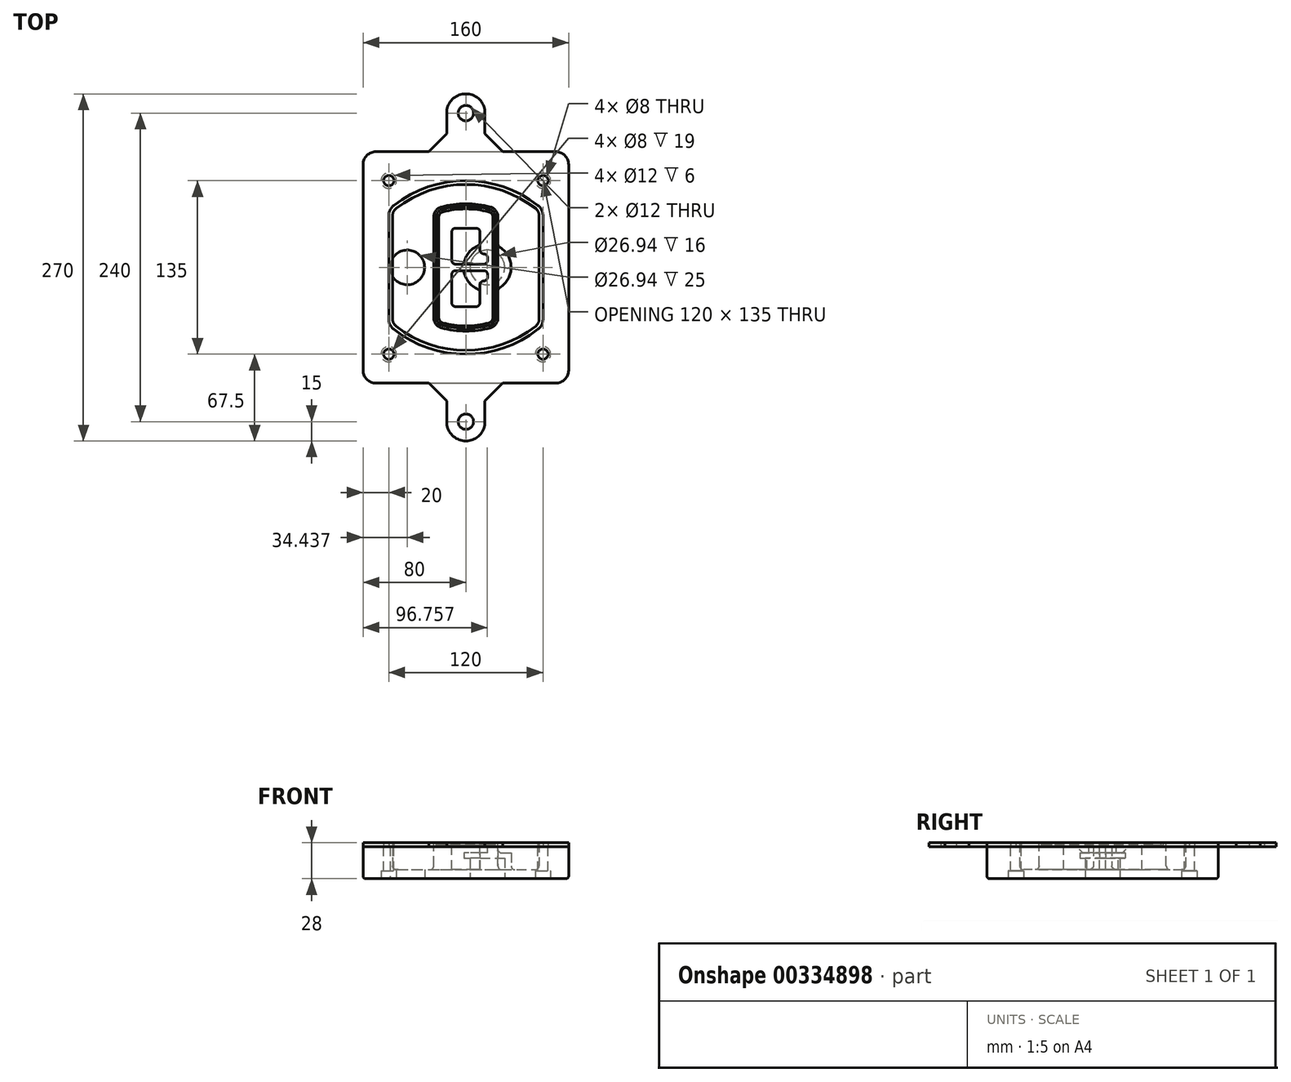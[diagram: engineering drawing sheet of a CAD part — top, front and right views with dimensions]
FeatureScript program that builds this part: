
annotation { "Feature Type Name" : "Feature", "Feature Type Description" : "" }
export const myFeature = defineFeature(function(context is Context, id is Id, definition is map)
    precondition{}
    {
        {
            var Q0;
            Q0=qCreatedBy(makeId("Top.planeOp"),FACE);
            var sketch = newSketch(context, id + "F0", { "sketchPlane" : qUnion([Q0])});
            skPoint(sketch, "E0.rect.middle", {"position": v(0, 0) * mm});
            skLineSegment(sketch, "E1.bottom", {"start": v(-70, -90) * mm, "end": v(70, -90) * mm});
            skLineSegment(sketch, "E1.top", {"start": v(-70, 90) * mm, "end": v(70, 90) * mm});
            skLineSegment(sketch, "E1.left", {"start": v(-80, -80) * mm, "end": v(-80, 80) * mm});
            skLineSegment(sketch, "E1.right", {"start": v(80, -80) * mm, "end": v(80, 80) * mm});
            skLineSegment(sketch, "E2", {"start": v(-80, 90) * mm, "end": v(80, -90) * mm, "construction": true});
            skLineSegment(sketch, "E3", {"start": v(80, 90) * mm, "end": v(-80, -90) * mm, "construction": true});
            skCircle(sketch, "E4", {"center": v(-60, 67.5) * mm, "radius": 4 * mm});
            skCircle(sketch, "E5", {"center": v(60, 67.5) * mm, "radius": 4 * mm});
            skCircle(sketch, "E6", {"center": v(60, -67.5) * mm, "radius": 4 * mm});
            skCircle(sketch, "E7", {"center": v(-60, -67.5) * mm, "radius": 4 * mm});
            skLineSegment(sketch, "E8", {"start": v(-60, 67.5) * mm, "end": v(60, 67.5) * mm, "construction": true});
            skLineSegment(sketch, "E9", {"start": v(60, 67.5) * mm, "end": v(60, -67.5) * mm, "construction": true});
            skLineSegment(sketch, "E10", {"start": v(60, -67.5) * mm, "end": v(-60, -67.5) * mm, "construction": true});
            skLineSegment(sketch, "E11", {"start": v(-60, -67.5) * mm, "end": v(-60, 67.5) * mm, "construction": true});
            skLineSegment(sketch, "E12", {"start": v(-60, 40.3) * mm, "end": v(-60, -40.3) * mm});
            skLineSegment(sketch, "E13", {"start": v(60, 40.3) * mm, "end": v(60, -40.3) * mm});
            skArc(sketch, "E14", {"start": v(56.15, 48.18) * mm, "mid": v(0, 67.5) * mm, "end": v(-56.15, 48.18) * mm});
            skArc(sketch, "E15", {"start": v(-56.15, -48.18) * mm, "mid": v(0, -67.5) * mm, "end": v(56.15, -48.18) * mm});
            skLineSegment(sketch, "E16", {"start": v(-60, 0) * mm, "end": v(60, 0) * mm, "construction": true});
            skPoint(sketch, "E17.visualSharp", {"position": v(-60, -45) * mm});
            skArc(sketch, "E17.filletArc", {"start": v(-60, -40.3) * mm, "mid": v(-58.99, -44.68) * mm, "end": v(-56.15, -48.18) * mm});
            skPoint(sketch, "E18.visualSharp", {"position": v(-60, 45) * mm});
            skArc(sketch, "E18.filletArc", {"start": v(-56.15, 48.18) * mm, "mid": v(-58.99, 44.68) * mm, "end": v(-60, 40.3) * mm});
            skPoint(sketch, "E19.visualSharp", {"position": v(60, 45) * mm});
            skArc(sketch, "E19.filletArc", {"start": v(60, 40.3) * mm, "mid": v(58.99, 44.68) * mm, "end": v(56.15, 48.18) * mm});
            skPoint(sketch, "E20.visualSharp", {"position": v(60, -45) * mm});
            skArc(sketch, "E20.filletArc", {"start": v(56.15, -48.18) * mm, "mid": v(58.99, -44.68) * mm, "end": v(60, -40.3) * mm});
            skPoint(sketch, "E21.visualSharp", {"position": v(-80, 90) * mm});
            skArc(sketch, "E21.filletArc", {"start": v(-70, 90) * mm, "mid": v(-77.07, 87.07) * mm, "end": v(-80, 80) * mm});
            skPoint(sketch, "E22.visualSharp", {"position": v(80, 90) * mm});
            skArc(sketch, "E22.filletArc", {"start": v(80, 80) * mm, "mid": v(77.07, 87.07) * mm, "end": v(70, 90) * mm});
            skPoint(sketch, "E23.visualSharp", {"position": v(80, -90) * mm});
            skArc(sketch, "E23.filletArc", {"start": v(70, -90) * mm, "mid": v(77.07, -87.07) * mm, "end": v(80, -80) * mm});
            skPoint(sketch, "E24.visualSharp", {"position": v(-80, -90) * mm});
            skArc(sketch, "E24.filletArc", {"start": v(-80, -80) * mm, "mid": v(-77.07, -87.07) * mm, "end": v(-70, -90) * mm});
            skArc(sketch, "E25.0", {"start": v(57, 40.3) * mm, "mid": v(56.3, 43.36) * mm, "end": v(54.3, 45.81) * mm});
            skLineSegment(sketch, "E25.1", {"start": v(57, 40.3) * mm, "end": v(57, -40.3) * mm});
            skArc(sketch, "E25.2", {"start": v(54.3, -45.81) * mm, "mid": v(56.3, -43.36) * mm, "end": v(57, -40.3) * mm});
            skArc(sketch, "E25.3", {"start": v(-54.3, -45.81) * mm, "mid": v(0, -64.5) * mm, "end": v(54.3, -45.81) * mm});
            skArc(sketch, "E25.4", {"start": v(-57, -40.3) * mm, "mid": v(-56.3, -43.36) * mm, "end": v(-54.3, -45.81) * mm});
            skArc(sketch, "E25.5", {"start": v(54.3, 45.81) * mm, "mid": v(0, 64.5) * mm, "end": v(-54.3, 45.81) * mm});
            skLineSegment(sketch, "E25.6", {"start": v(-57, 40.3) * mm, "end": v(-57, -40.3) * mm});
            skArc(sketch, "E25.7", {"start": v(-54.3, 45.81) * mm, "mid": v(-56.3, 43.36) * mm, "end": v(-57, 40.3) * mm});
            skArc(sketch, "E26.0", {"start": v(-58.62, 51.33) * mm, "mid": v(-62.58, 46.43) * mm, "end": v(-64, 40.3) * mm});
            skArc(sketch, "E26.1", {"start": v(58.62, 51.33) * mm, "mid": v(0, 71.5) * mm, "end": v(-58.62, 51.33) * mm});
            skArc(sketch, "E26.2", {"start": v(64, 40.3) * mm, "mid": v(62.58, 46.43) * mm, "end": v(58.62, 51.33) * mm});
            skLineSegment(sketch, "E26.3", {"start": v(64, 40.3) * mm, "end": v(64, -40.3) * mm});
            skArc(sketch, "E26.4", {"start": v(58.62, -51.33) * mm, "mid": v(62.58, -46.43) * mm, "end": v(64, -40.3) * mm});
            skLineSegment(sketch, "E26.5", {"start": v(-64, 40.3) * mm, "end": v(-64, -40.3) * mm});
            skArc(sketch, "E26.6", {"start": v(-58.62, -51.33) * mm, "mid": v(0, -71.5) * mm, "end": v(58.62, -51.33) * mm});
            skArc(sketch, "E26.7", {"start": v(-64, -40.3) * mm, "mid": v(-62.58, -46.43) * mm, "end": v(-58.62, -51.33) * mm});
            skSolve(sketch);
        }
        {
            var Q0;
            Q0=makeQuery(id+"F0.imprint","IMPRINT",FACE,{"disambiguationData":[TD([[makeQuery(id+"F0.imprint","IMPRINT",EDGE,{"derivedFrom":sQuery(id+"F0.wireOp",EDGE,"E1.bottom")}),1.0]])]});
            var Q1;
            Q1=makeQuery(id+"F0.imprint","IMPRINT",FACE,{"disambiguationData":[TD([[makeQuery(id+"F0.imprint","IMPRINT",EDGE,{"derivedFrom":sQuery(id+"F0.wireOp",EDGE,"E12")}),1.0]])]});
            var Q2;
            Q2=makeQuery(id+"F0.imprint","IMPRINT",FACE,{"disambiguationData":[TD([[makeQuery(id+"F0.imprint","IMPRINT",EDGE,{"derivedFrom":sQuery(id+"F0.wireOp",EDGE,"E25.0")}),1.0]])]});
            var Q3;
            Q3=makeQuery(id+"F0.imprint","IMPRINT",FACE,{"disambiguationData":[TD([[makeQuery(id+"F0.imprint","IMPRINT",EDGE,{"derivedFrom":sQuery(id+"F0.wireOp",EDGE,"E12")}),-1.0]])]});
            extrude(context, id + "F1", {"entities" : qUnion([Q0, Q1, Q2, Q3]), "oppositeDirection" : true, "depth" : 25 * mm});
        }
        {
            var Q0;
            Q0=makeQuery(id+"F0.imprint","IMPRINT",FACE,{"disambiguationData":[TD([[makeQuery(id+"F0.imprint","IMPRINT",EDGE,{"derivedFrom":sQuery(id+"F0.wireOp",EDGE,"E12")}),1.0]])]});
            extrude(context, id + "F2", {"entities" : qUnion([Q0]), "operationType" : NewBodyOperationType.ADD, "depth" : 3 * mm});
        }
        {
            var Q0;
            Q0=makeQuery(id+"F0.imprint","IMPRINT",FACE,{"disambiguationData":[TD([[makeQuery(id+"F0.imprint","IMPRINT",EDGE,{"derivedFrom":sQuery(id+"F0.wireOp",EDGE,"E25.0")}),1.0]])]});
            extrude(context, id + "F3", {"entities" : qUnion([Q0]), "operationType" : NewBodyOperationType.REMOVE, "oppositeDirection" : true, "depth" : 18 * mm});
        }
        {
            var Q0;
            Q0=makeQuery(id+"F2.opExtrude","CAP_FACE",FACE,{"disambiguationData":[OSD([sQuery(id+"F0.wireOp",EDGE,"E12"),sQuery(id+"F0.wireOp",EDGE,"E13"),sQuery(id+"F0.wireOp",EDGE,"E14"),sQuery(id+"F0.wireOp",EDGE,"E15"),sQuery(id+"F0.wireOp",EDGE,"E17.filletArc"),sQuery(id+"F0.wireOp",EDGE,"E18.filletArc"),sQuery(id+"F0.wireOp",EDGE,"E19.filletArc"),sQuery(id+"F0.wireOp",EDGE,"E20.filletArc"),sQuery(id+"F0.wireOp",EDGE,"E25.0"),sQuery(id+"F0.wireOp",EDGE,"E25.1"),sQuery(id+"F0.wireOp",EDGE,"E25.2"),sQuery(id+"F0.wireOp",EDGE,"E25.3"),sQuery(id+"F0.wireOp",EDGE,"E25.4"),sQuery(id+"F0.wireOp",EDGE,"E25.5"),sQuery(id+"F0.wireOp",EDGE,"E25.6"),sQuery(id+"F0.wireOp",EDGE,"E25.7")])],"isStart":false});
            var sketch = newSketch(context, id + "F4", { "sketchPlane" : qUnion([Q0])});
            skArc(sketch, "E27.0", {"start": v(-19.08, -46.97) * mm, "mid": v(0, -49.5) * mm, "end": v(19.08, -46.97) * mm});
            skArc(sketch, "E28.0", {"start": v(19.08, 46.97) * mm, "mid": v(0, 49.5) * mm, "end": v(-19.08, 46.97) * mm});
            skLineSegment(sketch, "E29", {"start": v(-25, 39.25) * mm, "end": v(-25, -39.25) * mm});
            skLineSegment(sketch, "E30", {"start": v(25, 39.25) * mm, "end": v(25, -39.25) * mm});
            skLineSegment(sketch, "E31", {"start": v(-25, 45.1) * mm, "end": v(25, 45.1) * mm, "construction": true});
            skLineSegment(sketch, "E32", {"start": v(-25, -45.1) * mm, "end": v(25, -45.1) * mm, "construction": true});
            skPoint(sketch, "E33.visualSharp", {"position": v(-25, 45.1) * mm});
            skArc(sketch, "E33.filletArc", {"start": v(-19.08, 46.97) * mm, "mid": v(-23.35, 44.11) * mm, "end": v(-25, 39.25) * mm});
            skPoint(sketch, "E34.visualSharp", {"position": v(25, 45.1) * mm});
            skArc(sketch, "E34.filletArc", {"start": v(25, 39.25) * mm, "mid": v(23.35, 44.11) * mm, "end": v(19.08, 46.97) * mm});
            skPoint(sketch, "E35.visualSharp", {"position": v(25, -45.1) * mm});
            skArc(sketch, "E35.filletArc", {"start": v(19.08, -46.97) * mm, "mid": v(23.35, -44.11) * mm, "end": v(25, -39.25) * mm});
            skPoint(sketch, "E36.visualSharp", {"position": v(-25, -45.1) * mm});
            skArc(sketch, "E36.filletArc", {"start": v(-25, -39.25) * mm, "mid": v(-23.35, -44.11) * mm, "end": v(-19.08, -46.97) * mm});
            skArc(sketch, "E37.0", {"start": v(54.3, 45.81) * mm, "mid": v(0, 64.5) * mm, "end": v(-54.3, 45.81) * mm});
            skArc(sketch, "E37.1", {"start": v(-54.3, 45.81) * mm, "mid": v(-56.3, 43.36) * mm, "end": v(-57, 40.3) * mm});
            skLineSegment(sketch, "E37.2", {"start": v(-57, 40.3) * mm, "end": v(-57, -40.3) * mm});
            skArc(sketch, "E37.3", {"start": v(-57, -40.3) * mm, "mid": v(-56.3, -43.36) * mm, "end": v(-54.3, -45.81) * mm});
            skArc(sketch, "E37.4", {"start": v(-54.3, -45.81) * mm, "mid": v(0, -64.5) * mm, "end": v(54.3, -45.81) * mm});
            skArc(sketch, "E37.5", {"start": v(54.3, -45.81) * mm, "mid": v(56.3, -43.36) * mm, "end": v(57, -40.3) * mm});
            skLineSegment(sketch, "E37.6", {"start": v(57, 40.3) * mm, "end": v(57, -40.3) * mm});
            skArc(sketch, "E37.7", {"start": v(57, 40.3) * mm, "mid": v(56.3, 43.36) * mm, "end": v(54.3, 45.81) * mm});
            skLineSegment(sketch, "E38.0", {"start": v(23, 39.25) * mm, "end": v(23, -39.25) * mm});
            skArc(sketch, "E38.1", {"start": v(18.56, -45.04) * mm, "mid": v(21.76, -42.9) * mm, "end": v(23, -39.25) * mm});
            skArc(sketch, "E38.2", {"start": v(-18.56, -45.04) * mm, "mid": v(0, -47.5) * mm, "end": v(18.56, -45.04) * mm});
            skArc(sketch, "E38.3", {"start": v(-23, -39.25) * mm, "mid": v(-21.76, -42.9) * mm, "end": v(-18.56, -45.04) * mm});
            skLineSegment(sketch, "E38.4", {"start": v(-23, 39.25) * mm, "end": v(-23, -39.25) * mm});
            skArc(sketch, "E38.5", {"start": v(23, 39.25) * mm, "mid": v(21.76, 42.9) * mm, "end": v(18.56, 45.04) * mm});
            skArc(sketch, "E38.6", {"start": v(-18.56, 45.04) * mm, "mid": v(-21.76, 42.9) * mm, "end": v(-23, 39.25) * mm});
            skArc(sketch, "E38.7", {"start": v(18.56, 45.04) * mm, "mid": v(0, 47.5) * mm, "end": v(-18.56, 45.04) * mm});
            skArc(sketch, "E39.0", {"start": v(21, 39.25) * mm, "mid": v(20.18, 41.68) * mm, "end": v(18.04, 43.1) * mm});
            skLineSegment(sketch, "E39.1", {"start": v(21, 39.25) * mm, "end": v(21, -39.25) * mm});
            skArc(sketch, "E39.2", {"start": v(18.04, -43.1) * mm, "mid": v(20.18, -41.68) * mm, "end": v(21, -39.25) * mm});
            skArc(sketch, "E39.3", {"start": v(-18.04, -43.1) * mm, "mid": v(0, -45.5) * mm, "end": v(18.04, -43.1) * mm});
            skArc(sketch, "E39.4", {"start": v(-21, -39.25) * mm, "mid": v(-20.18, -41.68) * mm, "end": v(-18.04, -43.1) * mm});
            skArc(sketch, "E39.5", {"start": v(18.04, 43.1) * mm, "mid": v(0, 45.5) * mm, "end": v(-18.04, 43.1) * mm});
            skLineSegment(sketch, "E39.6", {"start": v(-21, 39.25) * mm, "end": v(-21, -39.25) * mm});
            skArc(sketch, "E39.7", {"start": v(-18.04, 43.1) * mm, "mid": v(-20.18, 41.68) * mm, "end": v(-21, 39.25) * mm});
            skLineSegment(sketch, "E40", {"start": v(-25, 0) * mm, "end": v(25, 0) * mm, "construction": true});
            skLineSegment(sketch, "E41", {"start": v(-11, 5.5) * mm, "end": v(-11, 27.5) * mm});
            skLineSegment(sketch, "E42", {"start": v(-8, 30.5) * mm, "end": v(8, 30.5) * mm});
            skLineSegment(sketch, "E43", {"start": v(11, 27.5) * mm, "end": v(11, 13.5) * mm});
            skLineSegment(sketch, "E44", {"start": v(14, 10.5) * mm, "end": v(14, 10.5) * mm});
            skLineSegment(sketch, "E45", {"start": v(17, 7.5) * mm, "end": v(17, 5.5) * mm});
            skLineSegment(sketch, "E46", {"start": v(14, 2.5) * mm, "end": v(-8, 2.5) * mm});
            skPoint(sketch, "E47.visualSharp", {"position": v(-11, 30.5) * mm});
            skArc(sketch, "E47.filletArc", {"start": v(-8, 30.5) * mm, "mid": v(-10.12, 29.62) * mm, "end": v(-11, 27.5) * mm});
            skPoint(sketch, "E48.visualSharp", {"position": v(11, 30.5) * mm});
            skArc(sketch, "E48.filletArc", {"start": v(11, 27.5) * mm, "mid": v(10.12, 29.62) * mm, "end": v(8, 30.5) * mm});
            skPoint(sketch, "E49.visualSharp", {"position": v(11, 10.5) * mm});
            skArc(sketch, "E49.filletArc", {"start": v(11, 13.5) * mm, "mid": v(11.88, 11.38) * mm, "end": v(14, 10.5) * mm});
            skPoint(sketch, "E50.visualSharp", {"position": v(17, 10.5) * mm});
            skArc(sketch, "E50.filletArc", {"start": v(17, 7.5) * mm, "mid": v(16.12, 9.62) * mm, "end": v(14, 10.5) * mm});
            skPoint(sketch, "E51.visualSharp", {"position": v(17, 2.5) * mm});
            skArc(sketch, "E51.filletArc", {"start": v(14, 2.5) * mm, "mid": v(16.12, 3.38) * mm, "end": v(17, 5.5) * mm});
            skPoint(sketch, "E52.visualSharp", {"position": v(-11, 2.5) * mm});
            skArc(sketch, "E52.filletArc", {"start": v(-11, 5.5) * mm, "mid": v(-10.12, 3.38) * mm, "end": v(-8, 2.5) * mm});
            skLineSegment(sketch, "E53.0.MirrorCS", {"start": v(14, -2.5) * mm, "end": v(-8, -2.5) * mm});
            skArc(sketch, "E54.0.MirrorCS", {"start": v(-11, -5.5) * mm, "mid": v(-10.12, -3.38) * mm, "end": v(-8, -2.5) * mm});
            skLineSegment(sketch, "E55.0.MirrorCS", {"start": v(-11, -5.5) * mm, "end": v(-11, -27.5) * mm});
            skArc(sketch, "E56.0.MirrorCS", {"start": v(-8, -30.5) * mm, "mid": v(-10.12, -29.62) * mm, "end": v(-11, -27.5) * mm});
            skLineSegment(sketch, "E57.0.MirrorCS", {"start": v(-8, -30.5) * mm, "end": v(8, -30.5) * mm});
            skArc(sketch, "E58.0.MirrorCS", {"start": v(11, -27.5) * mm, "mid": v(10.12, -29.62) * mm, "end": v(8, -30.5) * mm});
            skLineSegment(sketch, "E59.0.MirrorCS", {"start": v(11, -27.5) * mm, "end": v(11, -13.5) * mm});
            skArc(sketch, "E60.0.MirrorCS", {"start": v(11, -13.5) * mm, "mid": v(11.88, -11.38) * mm, "end": v(14, -10.5) * mm});
            skArc(sketch, "E61.0.MirrorCS", {"start": v(17, -7.5) * mm, "mid": v(16.12, -9.62) * mm, "end": v(14, -10.5) * mm});
            skLineSegment(sketch, "E62.0.MirrorCS", {"start": v(17, -7.5) * mm, "end": v(17, -5.5) * mm});
            skArc(sketch, "E63.0.MirrorCS", {"start": v(14, -2.5) * mm, "mid": v(16.12, -3.38) * mm, "end": v(17, -5.5) * mm});
            skSolve(sketch);
        }
        {
            var Q0;
            Q0=makeQuery(id+"F4.imprint","IMPRINT",FACE,{"disambiguationData":[TD([[makeQuery(id+"F4.imprint","IMPRINT",EDGE,{"derivedFrom":sQuery(id+"F4.wireOp",EDGE,"E27.0")}),1.0]])]});
            var Q1;
            Q1=makeQuery(id+"F4.imprint","IMPRINT",FACE,{"disambiguationData":[TD([[makeQuery(id+"F4.imprint","IMPRINT",EDGE,{"derivedFrom":sQuery(id+"F4.wireOp",EDGE,"E38.0")}),-1.0]])]});
            var Q2;
            Q2=makeQuery(id+"F4.imprint","IMPRINT",FACE,{"disambiguationData":[TD([[makeQuery(id+"F4.imprint","IMPRINT",EDGE,{"derivedFrom":sQuery(id+"F4.wireOp",EDGE,"E39.0")}),1.0]])]});
            extrude(context, id + "F5", {"entities" : qUnion([Q0, Q1, Q2]), "operationType" : NewBodyOperationType.ADD, "endBound" : BoundingType.UP_TO_NEXT, "oppositeDirection" : true, "depth" : 25 * mm});
        }
        {
            var Q0;
            Q0=makeQuery(id+"F4.imprint","IMPRINT",FACE,{"disambiguationData":[TD([[makeQuery(id+"F4.imprint","IMPRINT",EDGE,{"derivedFrom":sQuery(id+"F4.wireOp",EDGE,"E38.0")}),-1.0]])]});
            extrude(context, id + "F6", {"entities" : qUnion([Q0]), "operationType" : NewBodyOperationType.REMOVE, "oppositeDirection" : true, "depth" : 2 * mm});
        }
        {
            var Q0;
            Q0=makeQuery(id+"F1.opExtrude","CAP_FACE",FACE,{"disambiguationData":[OSD([sQuery(id+"F0.wireOp",EDGE,"E1.bottom"),sQuery(id+"F0.wireOp",EDGE,"E1.top"),sQuery(id+"F0.wireOp",EDGE,"E1.left"),sQuery(id+"F0.wireOp",EDGE,"E1.right"),sQuery(id+"F0.wireOp",EDGE,"E4"),sQuery(id+"F0.wireOp",EDGE,"E5"),sQuery(id+"F0.wireOp",EDGE,"E6"),sQuery(id+"F0.wireOp",EDGE,"E7"),sQuery(id+"F0.wireOp",EDGE,"E21.filletArc"),sQuery(id+"F0.wireOp",EDGE,"E22.filletArc"),sQuery(id+"F0.wireOp",EDGE,"E23.filletArc"),sQuery(id+"F0.wireOp",EDGE,"E24.filletArc")])],"isStart":false});
            var sketch = newSketch(context, id + "F7", { "sketchPlane" : qUnion([Q0])});
            skCircle(sketch, "E64", {"center": v(16.76, 0) * mm, "radius": 13.47 * mm});
            skCircle(sketch, "E65", {"center": v(-45.56, 0) * mm, "radius": 13.47 * mm});
            skLineSegment(sketch, "E66", {"start": v(80, 0) * mm, "end": v(-80, 0) * mm});
            skCircle(sketch, "E67", {"center": v(16.76, 0) * mm, "radius": 18.47 * mm});
            skCircle(sketch, "E68", {"center": v(60, -67.5) * mm, "radius": 6 * mm});
            skCircle(sketch, "E69", {"center": v(-60, -67.5) * mm, "radius": 6 * mm});
            skCircle(sketch, "E70", {"center": v(-60, 67.5) * mm, "radius": 6 * mm});
            skCircle(sketch, "E71", {"center": v(60, 67.5) * mm, "radius": 6 * mm});
            skSolve(sketch);
        }
        {
            var Q0;
            {var subQ1=sQuery(id+"F7.wireOp",EDGE,"E66");var subQ4=sQuery(id+"F7.wireOp",EDGE,"E64");var subQ6=makeQuery(id+"F7.imprint","INTERSECT",VERTEX,{"disambiguationData":[OD(0.0)],"derivedFrom":[subQ4,subQ1]});Q0=makeQuery(id+"F7.imprint","IMPRINT",FACE,{"disambiguationData":[TD([[makeQuery(id+"F7.imprint","IMPRINT",EDGE,{"disambiguationData":[TD([[subQ6,-1.0]])],"derivedFrom":subQ4}),-1.0]])]});}
            var Q1;
            {var subQ0=sQuery(id+"F7.wireOp",EDGE,"E66");var subQ1=sQuery(id+"F7.wireOp",EDGE,"E64");var subQ3=makeQuery(id+"F7.imprint","INTERSECT",VERTEX,{"disambiguationData":[OD(0.0)],"derivedFrom":[subQ1,subQ0]});Q1=makeQuery(id+"F7.imprint","IMPRINT",FACE,{"disambiguationData":[TD([[makeQuery(id+"F7.imprint","IMPRINT",EDGE,{"disambiguationData":[TD([[subQ3,-1.0]])],"derivedFrom":subQ1}),1.0]])]});}
            var Q2;
            {var subQ0=sQuery(id+"F7.wireOp",EDGE,"E66");var subQ1=sQuery(id+"F7.wireOp",EDGE,"E64");var subQ3=makeQuery(id+"F7.imprint","INTERSECT",VERTEX,{"disambiguationData":[OD(0.0)],"derivedFrom":[subQ1,subQ0]});Q2=makeQuery(id+"F7.imprint","IMPRINT",FACE,{"disambiguationData":[TD([[makeQuery(id+"F7.imprint","IMPRINT",EDGE,{"disambiguationData":[TD([[subQ3,1.0]])],"derivedFrom":subQ1}),1.0]])]});}
            var Q3;
            {var subQ1=sQuery(id+"F7.wireOp",EDGE,"E66");var subQ4=sQuery(id+"F7.wireOp",EDGE,"E64");var subQ6=makeQuery(id+"F7.imprint","INTERSECT",VERTEX,{"disambiguationData":[OD(0.0)],"derivedFrom":[subQ4,subQ1]});Q3=makeQuery(id+"F7.imprint","IMPRINT",FACE,{"disambiguationData":[TD([[makeQuery(id+"F7.imprint","IMPRINT",EDGE,{"disambiguationData":[TD([[subQ6,1.0]])],"derivedFrom":subQ4}),-1.0]])]});}
            extrude(context, id + "F8", {"entities" : qUnion([Q0, Q1, Q2, Q3]), "operationType" : NewBodyOperationType.ADD, "oppositeDirection" : true, "depth" : 20 * mm});
        }
        {
            var Q0;
            {var subQ0=sQuery(id+"F7.wireOp",EDGE,"E66");var subQ1=sQuery(id+"F7.wireOp",EDGE,"E64");var subQ3=makeQuery(id+"F7.imprint","INTERSECT",VERTEX,{"disambiguationData":[OD(0.0)],"derivedFrom":[subQ1,subQ0]});Q0=makeQuery(id+"F7.imprint","IMPRINT",FACE,{"disambiguationData":[TD([[makeQuery(id+"F7.imprint","IMPRINT",EDGE,{"disambiguationData":[TD([[subQ3,-1.0]])],"derivedFrom":subQ1}),1.0]])]});}
            var Q1;
            {var subQ0=sQuery(id+"F7.wireOp",EDGE,"E66");var subQ1=sQuery(id+"F7.wireOp",EDGE,"E64");var subQ3=makeQuery(id+"F7.imprint","INTERSECT",VERTEX,{"disambiguationData":[OD(0.0)],"derivedFrom":[subQ1,subQ0]});Q1=makeQuery(id+"F7.imprint","IMPRINT",FACE,{"disambiguationData":[TD([[makeQuery(id+"F7.imprint","IMPRINT",EDGE,{"disambiguationData":[TD([[subQ3,1.0]])],"derivedFrom":subQ1}),1.0]])]});}
            extrude(context, id + "F9", {"entities" : qUnion([Q0, Q1]), "operationType" : NewBodyOperationType.REMOVE, "oppositeDirection" : true, "depth" : 16 * mm});
        }
        {
            var Q0;
            {var subQ0=sQuery(id+"F7.wireOp",EDGE,"E66");var subQ1=sQuery(id+"F7.wireOp",EDGE,"E65");var subQ3=makeQuery(id+"F7.imprint","INTERSECT",VERTEX,{"disambiguationData":[OD(0.0)],"derivedFrom":[subQ1,subQ0]});Q0=makeQuery(id+"F7.imprint","IMPRINT",FACE,{"disambiguationData":[TD([[makeQuery(id+"F7.imprint","IMPRINT",EDGE,{"disambiguationData":[TD([[subQ3,-1.0]])],"derivedFrom":subQ1}),1.0]])]});}
            var Q1;
            {var subQ0=sQuery(id+"F7.wireOp",EDGE,"E66");var subQ1=sQuery(id+"F7.wireOp",EDGE,"E65");var subQ3=makeQuery(id+"F7.imprint","INTERSECT",VERTEX,{"disambiguationData":[OD(0.0)],"derivedFrom":[subQ1,subQ0]});Q1=makeQuery(id+"F7.imprint","IMPRINT",FACE,{"disambiguationData":[TD([[makeQuery(id+"F7.imprint","IMPRINT",EDGE,{"disambiguationData":[TD([[subQ3,1.0]])],"derivedFrom":subQ1}),1.0]])]});}
            extrude(context, id + "F10", {"entities" : qUnion([Q0, Q1]), "operationType" : NewBodyOperationType.REMOVE, "oppositeDirection" : true, "depth" : 25 * mm});
        }
        {
            var Q0;
            Q0=makeQuery(id+"F7.imprint","IMPRINT",FACE,{"disambiguationData":[TD([[makeQuery(id+"F7.imprint","IMPRINT",EDGE,{"derivedFrom":sQuery(id+"F7.wireOp",EDGE,"E68")}),1.0]])]});
            var Q1;
            Q1=makeQuery(id+"F7.imprint","IMPRINT",FACE,{"disambiguationData":[TD([[makeQuery(id+"F7.imprint","IMPRINT",EDGE,{"derivedFrom":makeQuery(id+"F1.opExtrude","CAP_EDGE",EDGE,{"disambiguationData":[OSD([sQuery(id+"F0.wireOp",EDGE,"E5")])],"isStart":false})}),-1.0]])]});
            var Q2;
            Q2=makeQuery(id+"F7.imprint","IMPRINT",FACE,{"disambiguationData":[TD([[makeQuery(id+"F7.imprint","IMPRINT",EDGE,{"derivedFrom":sQuery(id+"F7.wireOp",EDGE,"E69")}),1.0]])]});
            var Q3;
            Q3=makeQuery(id+"F7.imprint","IMPRINT",FACE,{"disambiguationData":[TD([[makeQuery(id+"F7.imprint","IMPRINT",EDGE,{"derivedFrom":makeQuery(id+"F1.opExtrude","CAP_EDGE",EDGE,{"disambiguationData":[OSD([sQuery(id+"F0.wireOp",EDGE,"E4")])],"isStart":false})}),-1.0]])]});
            var Q4;
            Q4=makeQuery(id+"F7.imprint","IMPRINT",FACE,{"disambiguationData":[TD([[makeQuery(id+"F7.imprint","IMPRINT",EDGE,{"derivedFrom":sQuery(id+"F7.wireOp",EDGE,"E70")}),1.0]])]});
            var Q5;
            Q5=makeQuery(id+"F7.imprint","IMPRINT",FACE,{"disambiguationData":[TD([[makeQuery(id+"F7.imprint","IMPRINT",EDGE,{"derivedFrom":makeQuery(id+"F1.opExtrude","CAP_EDGE",EDGE,{"disambiguationData":[OSD([sQuery(id+"F0.wireOp",EDGE,"E7")])],"isStart":false})}),-1.0]])]});
            var Q6;
            Q6=makeQuery(id+"F7.imprint","IMPRINT",FACE,{"disambiguationData":[TD([[makeQuery(id+"F7.imprint","IMPRINT",EDGE,{"derivedFrom":sQuery(id+"F7.wireOp",EDGE,"E71")}),1.0]])]});
            var Q7;
            Q7=makeQuery(id+"F7.imprint","IMPRINT",FACE,{"disambiguationData":[TD([[makeQuery(id+"F7.imprint","IMPRINT",EDGE,{"derivedFrom":makeQuery(id+"F1.opExtrude","CAP_EDGE",EDGE,{"disambiguationData":[OSD([sQuery(id+"F0.wireOp",EDGE,"E6")])],"isStart":false})}),-1.0]])]});
            extrude(context, id + "F11", {"entities" : qUnion([Q0, Q1, Q2, Q3, Q4, Q5, Q6, Q7]), "operationType" : NewBodyOperationType.REMOVE, "oppositeDirection" : true, "depth" : 6 * mm});
        }
        {
            var Q0;
            Q0=makeQuery(id+"F9.boolean.opBoolean","COPY",FACE,{"derivedFrom":makeQuery(id+"F9.opExtrude","CAP_FACE",FACE,{"disambiguationData":[OSD([sQuery(id+"F7.wireOp",EDGE,"E64")])],"isStart":false})});
            var sketch = newSketch(context, id + "F12", { "sketchPlane" : qUnion([Q0])});
            skArc(sketch, "E72.0", {"start": v(11, 17.55) * mm, "mid": v(2.57, 11.82) * mm, "end": v(-1.54, 2.5) * mm});
            skArc(sketch, "E72.1", {"start": v(-1.54, -2.5) * mm, "mid": v(2.57, -11.82) * mm, "end": v(11, -17.55) * mm});
            skLineSegment(sketch, "E73", {"start": v(-1.54, -2.5) * mm, "end": v(14, -2.5) * mm});
            skLineSegment(sketch, "E74.0", {"start": v(14, 2.5) * mm, "end": v(-1.54, 2.5) * mm});
            skArc(sketch, "E74.1", {"start": v(14, 2.5) * mm, "mid": v(16.12, 3.38) * mm, "end": v(17, 5.5) * mm});
            skLineSegment(sketch, "E74.2", {"start": v(17, 7.5) * mm, "end": v(17, 5.5) * mm});
            skArc(sketch, "E74.3", {"start": v(17, 7.5) * mm, "mid": v(16.12, 9.62) * mm, "end": v(14, 10.5) * mm});
            skArc(sketch, "E74.4", {"start": v(11, 13.5) * mm, "mid": v(11.88, 11.38) * mm, "end": v(14, 10.5) * mm});
            skLineSegment(sketch, "E74.5", {"start": v(11, 17.55) * mm, "end": v(11, 13.5) * mm});
            skLineSegment(sketch, "E74.7", {"start": v(14, -2.5) * mm, "end": v(-1.54, -2.5) * mm});
            skArc(sketch, "E74.8", {"start": v(14, -2.5) * mm, "mid": v(16.12, -3.38) * mm, "end": v(17, -5.5) * mm});
            skLineSegment(sketch, "E74.9", {"start": v(17, -7.5) * mm, "end": v(17, -5.5) * mm});
            skArc(sketch, "E74.10", {"start": v(17, -7.5) * mm, "mid": v(16.12, -9.62) * mm, "end": v(14, -10.5) * mm});
            skArc(sketch, "E74.11", {"start": v(11, -13.5) * mm, "mid": v(11.88, -11.38) * mm, "end": v(14, -10.5) * mm});
            skLineSegment(sketch, "E74.12", {"start": v(11, -17.55) * mm, "end": v(11, -13.5) * mm});
            skPoint(sketch, "E75.orphan", {"position": v(11, -27.5) * mm});
            skPoint(sketch, "E76.orphan", {"position": v(-8, -2.5) * mm});
            skPoint(sketch, "E77.orphan", {"position": v(-8, 2.5) * mm});
            skPoint(sketch, "E78.orphan", {"position": v(11, 27.5) * mm});
            skSolve(sketch);
        }
        {
            var Q0;
            {var subQ7=sQuery(id+"F12.wireOp",EDGE,"E72.0");var subQ14=sQuery(id+"F12.wireOp",EDGE,"E72.1");var subQ16=sQuery(id+"F12.wireOp",EDGE,"E74.1");var subQ18=sQuery(id+"F12.wireOp",EDGE,"E74.8");Q0=qUnion([makeQuery(id+"F12.imprint","IMPRINT",FACE,{"disambiguationData":[TD([[makeQuery(id+"F12.imprint","IMPRINT",EDGE,{"derivedFrom":subQ7}),1.0]])]}),makeQuery(id+"F12.imprint","IMPRINT",FACE,{"disambiguationData":[TD([[makeQuery(id+"F12.imprint","IMPRINT",EDGE,{"derivedFrom":subQ14}),1.0]])]}),makeQuery(id+"F12.imprint","IMPRINT",FACE,{"disambiguationData":[TD([[makeQuery(id+"F12.imprint","IMPRINT",EDGE,{"derivedFrom":subQ16}),1.0]])]}),makeQuery(id+"F12.imprint","IMPRINT",FACE,{"disambiguationData":[TD([[makeQuery(id+"F12.imprint","IMPRINT",EDGE,{"derivedFrom":subQ18}),-1.0]])]})]);}
            var Q1;
            Q1=makeQuery(id+"F5.boolean.opBoolean","SPLIT",FACE,{"disambiguationData":[TD([makeQuery(id+"F5.opExtrude","SWEPT_FACE",FACE,{"disambiguationData":[OSD([sQuery(id+"F4.wireOp",EDGE,"E41")])]})])],"derivedFrom":makeQuery(id+"F3.boolean.opBoolean","COPY",FACE,{"derivedFrom":makeQuery(id+"F3.opExtrude","CAP_FACE",FACE,{"disambiguationData":[OSD([sQuery(id+"F0.wireOp",EDGE,"E25.0"),sQuery(id+"F0.wireOp",EDGE,"E25.1"),sQuery(id+"F0.wireOp",EDGE,"E25.2"),sQuery(id+"F0.wireOp",EDGE,"E25.3"),sQuery(id+"F0.wireOp",EDGE,"E25.4"),sQuery(id+"F0.wireOp",EDGE,"E25.5"),sQuery(id+"F0.wireOp",EDGE,"E25.6"),sQuery(id+"F0.wireOp",EDGE,"E25.7")])],"isStart":false})})});
            extrude(context, id + "F13", {"entities" : qUnion([Q0]), "operationType" : NewBodyOperationType.REMOVE, "endBound" : BoundingType.UP_TO_SURFACE, "endBoundEntityFace" : qUnion([Q1]), "depth" : 25 * mm});
        }
        {
            var Q0;
            Q0=makeQuery(id+"F3.boolean.opBoolean","COPY",EDGE,{"derivedFrom":makeQuery(id+"F3.opExtrude","CAP_EDGE",EDGE,{"disambiguationData":[OSD([sQuery(id+"F0.wireOp",EDGE,"E25.6")])],"isStart":false})});
            var Q1;
            Q1=makeQuery(id+"F8.boolean.opBoolean","INTERSECT",EDGE,{"derivedFrom":[makeQuery(id+"F5.opExtrude","SWEPT_FACE",FACE,{"disambiguationData":[OSD([sQuery(id+"F4.wireOp",EDGE,"E30")])]}),makeQuery(id+"F8.opExtrude","CAP_FACE",FACE,{"disambiguationData":[OSD([sQuery(id+"F7.wireOp",EDGE,"E67")])],"isStart":false})]});
            var Q2;
            Q2=makeQuery(id+"F8.boolean.opBoolean","INTERSECT",EDGE,{"disambiguationData":[OD(1.0)],"derivedFrom":[makeQuery(id+"F5.opExtrude","SWEPT_FACE",FACE,{"disambiguationData":[OSD([sQuery(id+"F4.wireOp",EDGE,"E30")])]}),makeQuery(id+"F8.opExtrude","SWEPT_FACE",FACE,{"disambiguationData":[OSD([sQuery(id+"F7.wireOp",EDGE,"E67")])]})]});
            var Q3;
            {var subQ0=sQuery(id+"F4.wireOp",EDGE,"E30");Q3=makeQuery(id+"F8.boolean.opBoolean","SPLIT",EDGE,{"disambiguationData":[TD([makeQuery(id+"F5.opExtrude","SWEPT_FACE",FACE,{"disambiguationData":[OSD([sQuery(id+"F4.wireOp",EDGE,"E35.filletArc")])]})])],"derivedFrom":makeQuery(id+"F5.opExtrude","CAP_EDGE",EDGE,{"disambiguationData":[OSD([subQ0])],"isStart":false})});}
            var Q4;
            {var subQ0=sQuery(id+"F0.wireOp",EDGE,"E25.7");var subQ1=sQuery(id+"F0.wireOp",EDGE,"E25.1");var subQ2=sQuery(id+"F0.wireOp",EDGE,"E25.6");var subQ3=sQuery(id+"F0.wireOp",EDGE,"E25.5");var subQ4=sQuery(id+"F0.wireOp",EDGE,"E25.4");var subQ5=sQuery(id+"F0.wireOp",EDGE,"E25.0");var subQ6=sQuery(id+"F0.wireOp",EDGE,"E25.2");var subQ7=sQuery(id+"F0.wireOp",EDGE,"E25.3");Q4=makeQuery(id+"F8.boolean.opBoolean","INTERSECT",EDGE,{"derivedFrom":[makeQuery(id+"F5.boolean.opBoolean","SPLIT",FACE,{"disambiguationData":[TD([makeQuery(id+"F2.opExtrude","SWEPT_FACE",FACE,{"disambiguationData":[OSD([subQ5])]})])],"derivedFrom":makeQuery(id+"F3.boolean.opBoolean","COPY",FACE,{"derivedFrom":makeQuery(id+"F3.opExtrude","CAP_FACE",FACE,{"disambiguationData":[OSD([subQ5,subQ1,subQ6,subQ7,subQ4,subQ3,subQ2,subQ0])],"isStart":false})})}),makeQuery(id+"F8.opExtrude","SWEPT_FACE",FACE,{"disambiguationData":[OSD([sQuery(id+"F7.wireOp",EDGE,"E67")])]})]});}
            var Q5;
            Q5=makeQuery(id+"F8.boolean.opBoolean","INTERSECT",EDGE,{"disambiguationData":[OD(0.0)],"derivedFrom":[makeQuery(id+"F5.opExtrude","SWEPT_FACE",FACE,{"disambiguationData":[OSD([sQuery(id+"F4.wireOp",EDGE,"E30")])]}),makeQuery(id+"F8.opExtrude","SWEPT_FACE",FACE,{"disambiguationData":[OSD([sQuery(id+"F7.wireOp",EDGE,"E67")])]})]});
            fillet(context, id + "F14", {"entities" : qUnion([Q0, Q1, Q2, Q3, Q4, Q5]), "radius" : 3 * mm, "tangentPropagation" : true, "allowEdgeOverflow" : false});
        }
        {
            var Q0;
            Q0=makeQuery(id+"F1.opExtrude","CAP_EDGE",EDGE,{"disambiguationData":[OSD([sQuery(id+"F0.wireOp",EDGE,"E1.bottom")])],"isStart":false});
            fillet(context, id + "F15", {"entities" : qUnion([Q0]), "radius" : 2 * mm, "tangentPropagation" : true, "allowEdgeOverflow" : false});
        }
        {
            var Q0;
            {var subQ0=sQuery(id+"F0.wireOp",EDGE,"E21.filletArc");var subQ1=sQuery(id+"F0.wireOp",EDGE,"E7");var subQ2=sQuery(id+"F0.wireOp",EDGE,"E6");var subQ3=sQuery(id+"F0.wireOp",EDGE,"E5");var subQ4=sQuery(id+"F0.wireOp",EDGE,"E4");var subQ5=sQuery(id+"F0.wireOp",EDGE,"E22.filletArc");var subQ6=sQuery(id+"F0.wireOp",EDGE,"E1.bottom");var subQ7=sQuery(id+"F0.wireOp",EDGE,"E1.right");var subQ8=sQuery(id+"F0.wireOp",EDGE,"E1.top");var subQ9=sQuery(id+"F0.wireOp",EDGE,"E1.left");var subQ10=sQuery(id+"F0.wireOp",EDGE,"E23.filletArc");var subQ11=sQuery(id+"F0.wireOp",EDGE,"E24.filletArc");Q0=makeQuery(id+"F2.boolean.opBoolean","SPLIT",FACE,{"disambiguationData":[TD([makeQuery(id+"F1.opExtrude","SWEPT_FACE",FACE,{"disambiguationData":[OSD([subQ6])]})])],"derivedFrom":makeQuery(id+"F1.opExtrude","CAP_FACE",FACE,{"disambiguationData":[OSD([subQ6,subQ8,subQ9,subQ7,subQ4,subQ3,subQ2,subQ1,subQ0,subQ5,subQ10,subQ11])],"isStart":true})});}
            var sketch = newSketch(context, id + "F16", { "sketchPlane" : qUnion([Q0])});
            skLineSegment(sketch, "E79", {"start": v(28.77, 90) * mm, "end": v(14.75, 104.02) * mm});
            skLineSegment(sketch, "E80", {"start": v(14.75, 104.02) * mm, "end": v(14.75, 122.72) * mm});
            skLineSegment(sketch, "E81", {"start": v(-15, 108) * mm, "end": v(-15, 120) * mm});
            skArc(sketch, "E82", {"start": v(14.75, 122.72) * mm, "mid": v(-1.36, 134.94) * mm, "end": v(-15, 120) * mm});
            skCircle(sketch, "E83", {"center": v(0, 120) * mm, "radius": 6 * mm});
            skLineSegment(sketch, "E84", {"start": v(0, 120) * mm, "end": v(0, 90) * mm, "construction": true});
            skLineSegment(sketch, "E85.MirrorCS", {"start": v(-14.75, 104.02) * mm, "end": v(-14.75, 122.72) * mm});
            skArc(sketch, "E86.MirrorCS", {"start": v(-14.75, 122.72) * mm, "mid": v(1.36, 134.94) * mm, "end": v(15, 120) * mm});
            skLineSegment(sketch, "E87.MirrorCS", {"start": v(-28.77, 90) * mm, "end": v(-14.75, 104.02) * mm});
            skLineSegment(sketch, "E88", {"start": v(-80, 0) * mm, "end": v(80, 0) * mm, "construction": true});
            skLineSegment(sketch, "E89.MirrorCS", {"start": v(0, -120) * mm, "end": v(0, -90) * mm, "construction": true});
            skCircle(sketch, "E90.MirrorC", {"center": v(0, -120) * mm, "radius": 6 * mm});
            skLineSegment(sketch, "E91.MirrorCS", {"start": v(14.75, -104.02) * mm, "end": v(14.75, -122.72) * mm});
            skLineSegment(sketch, "E92.MirrorCS", {"start": v(28.77, -90) * mm, "end": v(14.75, -104.02) * mm});
            skArc(sketch, "E93.MirrorCS", {"start": v(14.75, -122.72) * mm, "mid": v(-1.36, -134.94) * mm, "end": v(-15, -120) * mm});
            skArc(sketch, "E94.MirrorCS", {"start": v(-14.75, -122.72) * mm, "mid": v(1.36, -134.94) * mm, "end": v(15, -120) * mm});
            skLineSegment(sketch, "E95.MirrorCS", {"start": v(-28.77, -90) * mm, "end": v(-14.75, -104.02) * mm});
            skLineSegment(sketch, "E96.MirrorCS", {"start": v(-14.75, -104.02) * mm, "end": v(-14.75, -122.72) * mm});
            skSolve(sketch);
        }
        {
            var Q0;
            {var subQ4=sQuery(id+"F16.wireOp",EDGE,"E80");Q0=makeQuery(id+"F16.imprint","IMPRINT",FACE,{"disambiguationData":[TD([[makeQuery(id+"F16.imprint","IMPRINT",EDGE,{"derivedFrom":subQ4}),1.0]])]});}
            var Q1;
            Q1=makeQuery(id+"F16.imprint","IMPRINT",FACE,{"disambiguationData":[TD([[makeQuery(id+"F16.imprint","IMPRINT",EDGE,{"derivedFrom":makeQuery(id+"F1.opExtrude","CAP_EDGE",EDGE,{"disambiguationData":[OSD([sQuery(id+"F0.wireOp",EDGE,"E1.left")])],"isStart":true})}),-1.0]])]});
            var Q2;
            {var subQ3=sQuery(id+"F16.wireOp",EDGE,"E91.MirrorCS");Q2=makeQuery(id+"F16.imprint","IMPRINT",FACE,{"disambiguationData":[TD([[makeQuery(id+"F16.imprint","IMPRINT",EDGE,{"derivedFrom":subQ3}),-1.0]])]});}
            var Q3;
            Q3=makeQuery(id+"F2.opExtrude","CAP_FACE",FACE,{"disambiguationData":[OSD([sQuery(id+"F0.wireOp",EDGE,"E12"),sQuery(id+"F0.wireOp",EDGE,"E13"),sQuery(id+"F0.wireOp",EDGE,"E14"),sQuery(id+"F0.wireOp",EDGE,"E15"),sQuery(id+"F0.wireOp",EDGE,"E17.filletArc"),sQuery(id+"F0.wireOp",EDGE,"E18.filletArc"),sQuery(id+"F0.wireOp",EDGE,"E19.filletArc"),sQuery(id+"F0.wireOp",EDGE,"E20.filletArc"),sQuery(id+"F0.wireOp",EDGE,"E25.0"),sQuery(id+"F0.wireOp",EDGE,"E25.1"),sQuery(id+"F0.wireOp",EDGE,"E25.2"),sQuery(id+"F0.wireOp",EDGE,"E25.3"),sQuery(id+"F0.wireOp",EDGE,"E25.4"),sQuery(id+"F0.wireOp",EDGE,"E25.5"),sQuery(id+"F0.wireOp",EDGE,"E25.6"),sQuery(id+"F0.wireOp",EDGE,"E25.7")])],"isStart":false});
            extrude(context, id + "F17", {"entities" : qUnion([Q0, Q1, Q2]), "endBound" : BoundingType.UP_TO_SURFACE, "endBoundEntityFace" : qUnion([Q3]), "depth" : 25 * mm});
        }
    });
